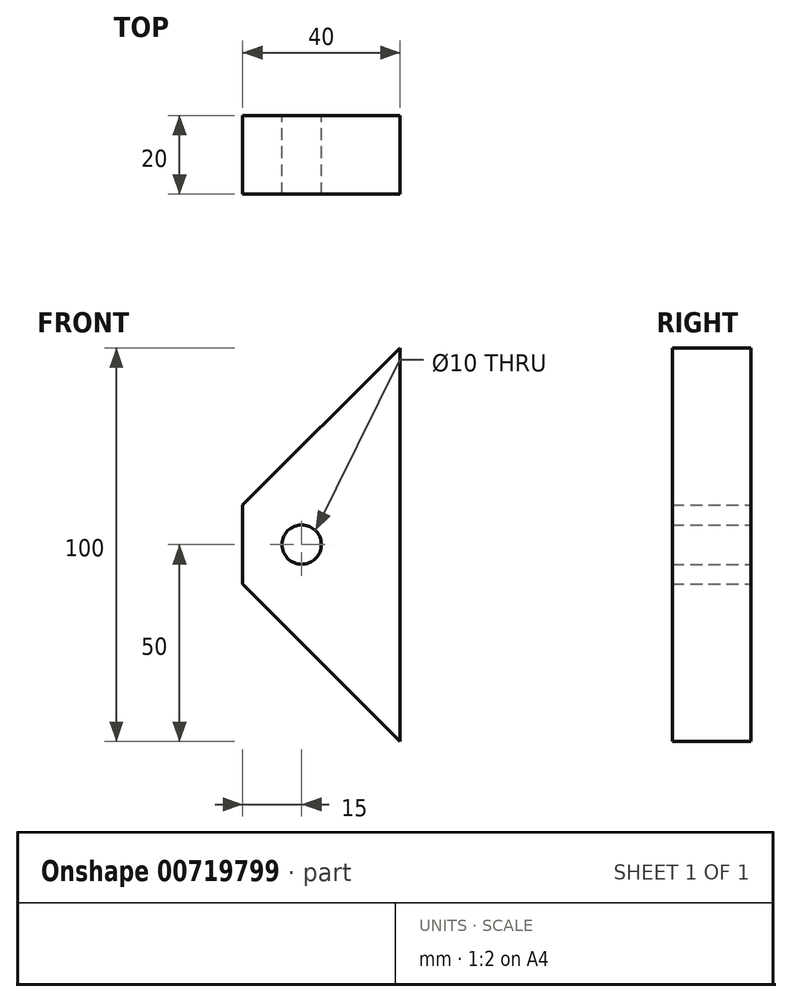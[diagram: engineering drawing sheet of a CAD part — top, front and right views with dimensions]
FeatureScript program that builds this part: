
annotation { "Feature Type Name" : "Feature", "Feature Type Description" : "" }
export const myFeature = defineFeature(function(context is Context, id is Id, definition is map)
    precondition{}
    {
        {
            var Q0;
            Q0=qCreatedBy(makeId("Front.planeOp"),FACE);
            var sketch = newSketch(context, id + "F0", { "sketchPlane" : qUnion([Q0])});
            skLineSegment(sketch, "E0", {"start": v(0, 0) * mm, "end": v(0, 50) * mm});
            skLineSegment(sketch, "E1", {"start": v(0, 50) * mm, "end": v(-40, 10) * mm});
            skLineSegment(sketch, "E2", {"start": v(-40, 10) * mm, "end": v(-40, 0) * mm});
            skLineSegment(sketch, "E3", {"start": v(7.2, 0) * mm, "end": v(-53.9, 0) * mm, "construction": true});
            skLineSegment(sketch, "E4.MirrorCS", {"start": v(-40, -10) * mm, "end": v(-40, 0) * mm});
            skLineSegment(sketch, "E5.MirrorCS", {"start": v(0, 0) * mm, "end": v(0, -50) * mm});
            skLineSegment(sketch, "E6.MirrorCS", {"start": v(0, -50) * mm, "end": v(-40, -10) * mm});
            skCircle(sketch, "E7", {"center": v(-25, 0) * mm, "radius": 5 * mm});
            skSolve(sketch);
        }
        {
            var Q0;
            Q0=makeQuery(id+"F0.imprint","IMPRINT",FACE,{"disambiguationData":[TD([[makeQuery(id+"F0.imprint","IMPRINT",EDGE,{"derivedFrom":sQuery(id+"F0.wireOp",EDGE,"E0")}),1.0]])]});
            extrude(context, id + "F1", {"entities" : qUnion([Q0]), "depth" : 10 * mm, "offsetDistance" : 25 * mm, "hasSecondDirection" : true, "secondDirectionOppositeDirection" : true, "secondDirectionDepth" : 10 * mm});
        }
    });
